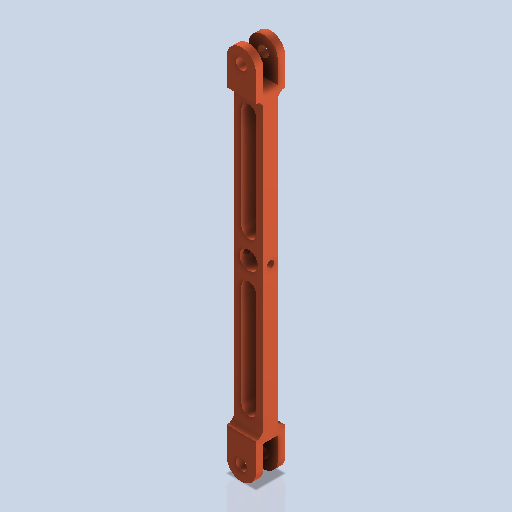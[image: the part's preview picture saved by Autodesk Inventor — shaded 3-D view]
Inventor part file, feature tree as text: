
AUTODESK INVENTOR PART (.ipt)
format: ipt  version: 2024.2 (Build 282272000, 272)  size: 383,488 bytes
history: native  units: mm
features: sketch x8, extrude x5, mirror x3, hole x3, fillet x2, plane x2
ambient origin geometry x8: Origin, YZ Plane, XZ Plane, XY Plane, X Axis, Y Axis, Z Axis, Center Point
bodies: Volumenkörper1 (feature_tree)
feature tree (23):
  extrude  "Extrusion1"  Depth=32.0mm
  extrude  "Extrusion2"  Depth=32.0mm TaperAngle=0.0deg
  extrude  "Extrusion4"  Depth=16.0mm
  fillet  "Rundung2"  Radius=40.0mm
  plane  "Arbeitsebene1"
  mirror  "Spiegeln1"
  fillet  "Rundung4"  Radius=10.0mm
  hole  "Bohrung3"  [1 undecoded]
  extrude  "Extrusion5"  Depth=16.0mm
  hole  "Bohrung4"  [1 undecoded]
  hole  "Bohrung5"  [1 undecoded]
  extrude  "Extrusion6"  Depth=16.0mm
  plane  "Arbeitsebene2"
  mirror  "Spiegeln2"
  mirror  "Spiegeln3"
  sketch  "Skizze1"  dims[d0=46.0mm d1=32.0mm]
  sketch  "Skizze2"  dims[d2=32.0mm d3=0.0mm d6=160.0mm d7=0.0mm]
  sketch  "Skizze4"  dims[d13=0.0mm d14=16.0mm d15=40.0mm d16=10.0mm d17=0.0mm]
  sketch  "Skizze7"  dims[d18=8.0mm]
  sketch  "Skizze8"  dims[d35=8.0mm d36=6.0mm d37=4.0mm d38=2.0mm d39=90.0deg d40=8.0mm d41=0.0mm d43=112.0mm]
  sketch  "Skizze9"  dims[d46=112.0mm d47=16.0mm]
  sketch  "Skizze10"  dims[d48=16.0mm d49=160.0mm d50=0.0mm]
  sketch  "Skizze11"  dims[d51=16.0mm d52=8.0mm d55=28.0mm d56=28.0mm d57=12.0mm d58=6.0mm d59=4.0mm d60=2.0mm d61=90.0deg d62=8.0mm d63=20.594885mm d64=50.0mm d65=50.0mm d66=20.0mm d67=6.0mm d68=4.0mm d69=2.0mm d70=90.0deg d71=8.0mm d72=20.594885mm d73=16.0mm d74=50.0mm d75=10.0mm d76=0.0mm d79=16.0mm]
note: 3 required parameter values undecoded (feature->parameter linkage not recoverable at this tier; creation-order binding heuristic only, values carry confidence <= 0.55)
